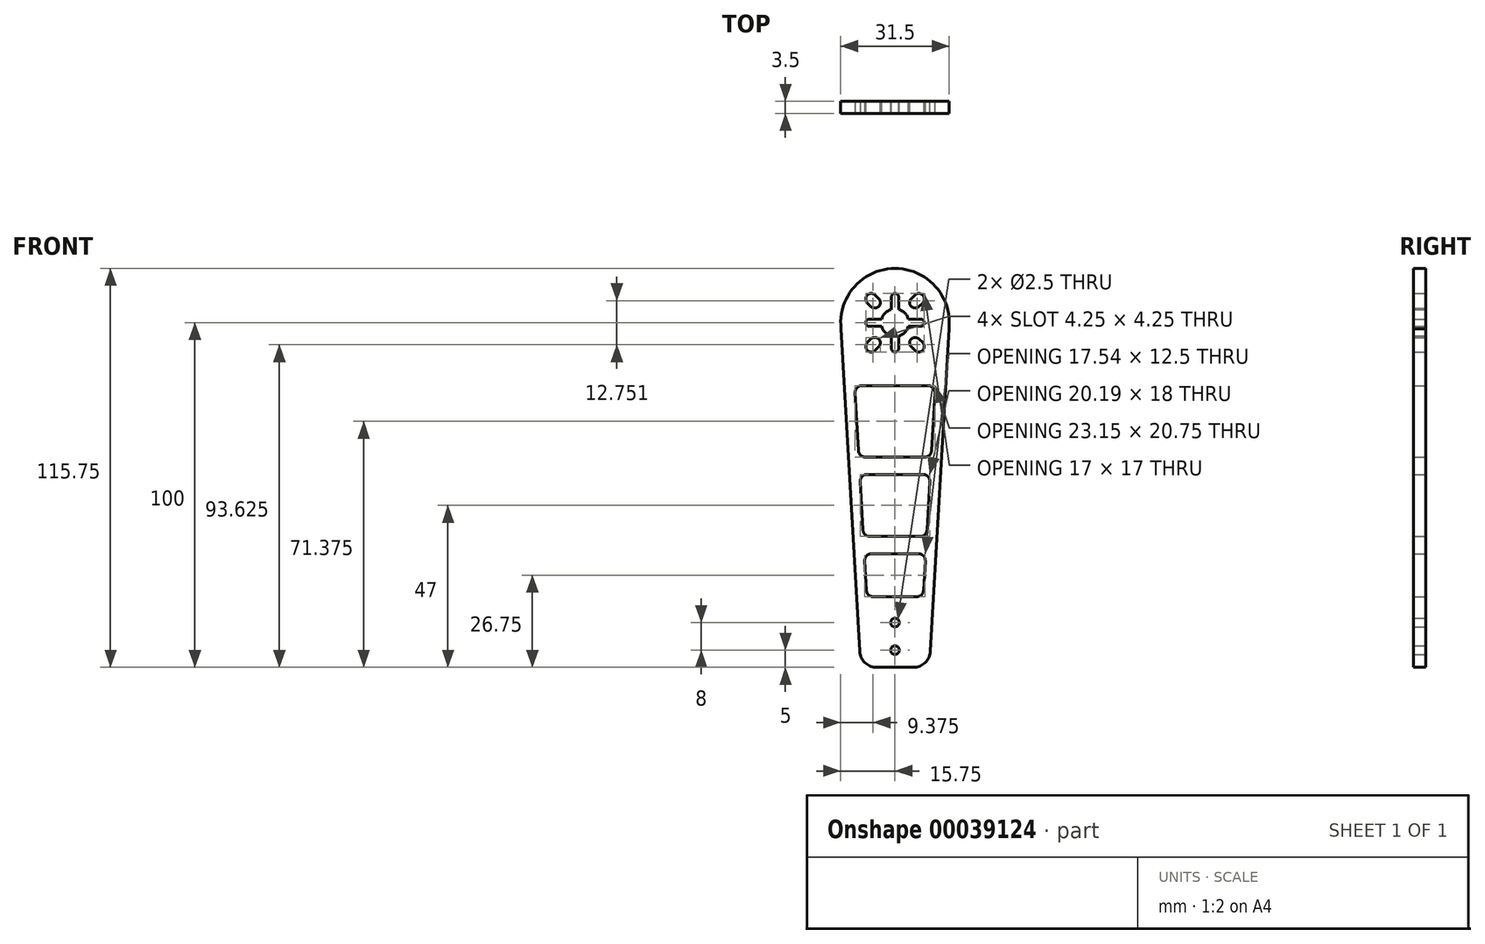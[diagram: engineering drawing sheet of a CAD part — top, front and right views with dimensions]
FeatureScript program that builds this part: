
annotation { "Feature Type Name" : "Feature", "Feature Type Description" : "" }
export const myFeature = defineFeature(function(context is Context, id is Id, definition is map)
    precondition{}
    {
        {
            var Q0;
            Q0=qCreatedBy(makeId("Front.planeOp"),FACE);
            var sketch = newSketch(context, id + "F0", { "sketchPlane" : qUnion([Q0])});
            skLineSegment(sketch, "E0", {"start": v(0, 21.72) * mm, "end": v(0, -118.47) * mm, "construction": true});
            skCircle(sketch, "E1", {"center": v(0, -87) * mm, "radius": 1.25 * mm});
            skCircle(sketch, "E2", {"center": v(0, -95) * mm, "radius": 1.25 * mm});
            skPoint(sketch, "E3.rect.middle", {"position": v(0, 0) * mm});
            skLineSegment(sketch, "E4", {"start": v(0, 0) * mm, "end": v(8.03, 8.03) * mm, "construction": true});
            skPoint(sketch, "E5.2.0", {"position": v(-6.38, -6.38) * mm});
            skPoint(sketch, "E6.rect.middle", {"position": v(6.38, 6.38) * mm});
            skLineSegment(sketch, "E7.rect.top", {"start": v(7.45, 1.05) * mm, "end": v(-7.45, 1.05) * mm});
            skLineSegment(sketch, "E7.rect.bottom", {"start": v(7.45, -1.05) * mm, "end": v(-7.45, -1.05) * mm});
            skLineSegment(sketch, "E8", {"start": v(-9.34, 0) * mm, "end": v(12.16, 0) * mm, "construction": true});
            skCircle(sketch, "E9", {"center": v(0, 0) * mm, "radius": 4 * mm});
            skPoint(sketch, "E5.1.0", {"position": v(-6.38, 6.38) * mm});
            skCircle(sketch, "E10", {"center": v(0, 0) * mm, "radius": 15.75 * mm});
            skLineSegment(sketch, "E3.rect.right", {"start": v(1.05, 7.45) * mm, "end": v(1.05, -7.45) * mm});
            skLineSegment(sketch, "E3.rect.left", {"start": v(-1.05, 7.45) * mm, "end": v(-1.05, -7.45) * mm});
            skPoint(sketch, "E5.3.0", {"position": v(6.38, -6.38) * mm});
            skArc(sketch, "E5.3.2", {"start": v(5.77, -8.03) * mm, "mid": v(8.03, -8.03) * mm, "end": v(8.03, -5.77) * mm});
            skLineSegment(sketch, "E11", {"start": v(0, 8.5) * mm, "end": v(12.03, 8.5) * mm, "construction": true});
            skArc(sketch, "E5.3.1", {"start": v(6.98, -4.72) * mm, "mid": v(4.72, -4.72) * mm, "end": v(4.72, -6.98) * mm});
            skArc(sketch, "E5.1.2", {"start": v(-5.77, 8.03) * mm, "mid": v(-8.03, 8.03) * mm, "end": v(-8.03, 5.77) * mm});
            skArc(sketch, "E5.2.2", {"start": v(-8.03, -5.77) * mm, "mid": v(-8.03, -8.03) * mm, "end": v(-5.77, -8.03) * mm});
            skArc(sketch, "E5.1.1", {"start": v(-6.98, 4.72) * mm, "mid": v(-4.72, 4.72) * mm, "end": v(-4.72, 6.98) * mm});
            skArc(sketch, "E12", {"start": v(4.72, 6.98) * mm, "mid": v(4.72, 4.72) * mm, "end": v(6.98, 4.72) * mm});
            skArc(sketch, "E5.2.1", {"start": v(-4.72, -6.98) * mm, "mid": v(-4.72, -4.72) * mm, "end": v(-6.98, -4.72) * mm});
            skArc(sketch, "E13", {"start": v(8.03, 5.77) * mm, "mid": v(8.03, 8.03) * mm, "end": v(5.77, 8.03) * mm});
            skLineSegment(sketch, "E5.1.6", {"start": v(-4.72, 6.98) * mm, "end": v(-5.77, 8.03) * mm});
            skArc(sketch, "E14", {"start": v(-1.05, -7.45) * mm, "mid": v(0, -8.5) * mm, "end": v(1.05, -7.45) * mm});
            skLineSegment(sketch, "E5.2.4", {"start": v(-6.98, -4.72) * mm, "end": v(-4.72, -6.98) * mm});
            skLineSegment(sketch, "E5.1.3", {"start": v(-5.77, 8.03) * mm, "end": v(-8.03, 5.77) * mm});
            skLineSegment(sketch, "E6.rect.bottom", {"start": v(6.98, 4.72) * mm, "end": v(8.03, 5.77) * mm});
            skLineSegment(sketch, "E6.rect.right", {"start": v(8.03, 5.77) * mm, "end": v(5.77, 8.03) * mm});
            skLineSegment(sketch, "E5.1.5", {"start": v(-6.98, 4.72) * mm, "end": v(-8.03, 5.77) * mm});
            skArc(sketch, "E15", {"start": v(1.05, 7.45) * mm, "mid": v(0, 8.5) * mm, "end": v(-1.05, 7.45) * mm});
            skLineSegment(sketch, "E5.2.3", {"start": v(-8.03, -5.77) * mm, "end": v(-5.77, -8.03) * mm});
            skLineSegment(sketch, "E5.3.6", {"start": v(4.72, -6.98) * mm, "end": v(5.77, -8.03) * mm});
            skLineSegment(sketch, "E6.rect.left", {"start": v(6.98, 4.72) * mm, "end": v(4.72, 6.98) * mm});
            skLineSegment(sketch, "E5.2.6", {"start": v(-6.98, -4.72) * mm, "end": v(-8.03, -5.77) * mm});
            skLineSegment(sketch, "E5.3.4", {"start": v(4.72, -6.98) * mm, "end": v(6.98, -4.72) * mm});
            skLineSegment(sketch, "E5.1.4", {"start": v(-4.72, 6.98) * mm, "end": v(-6.98, 4.72) * mm});
            skArc(sketch, "E16", {"start": v(7.45, -1.05) * mm, "mid": v(8.5, 0) * mm, "end": v(7.45, 1.05) * mm});
            skLineSegment(sketch, "E5.3.5", {"start": v(6.98, -4.72) * mm, "end": v(8.03, -5.77) * mm});
            skLineSegment(sketch, "E5.2.5", {"start": v(-4.72, -6.98) * mm, "end": v(-5.77, -8.03) * mm});
            skLineSegment(sketch, "E5.3.3", {"start": v(5.77, -8.03) * mm, "end": v(8.03, -5.77) * mm});
            skLineSegment(sketch, "E3.rect.top", {"start": v(-1.05, -7.45) * mm, "end": v(1.05, -7.45) * mm});
            skLineSegment(sketch, "E7.rect.right", {"start": v(-7.45, -1.05) * mm, "end": v(-7.45, 1.05) * mm});
            skLineSegment(sketch, "E7.rect.left", {"start": v(7.45, -1.05) * mm, "end": v(7.45, 1.05) * mm});
            skArc(sketch, "E17", {"start": v(-7.45, 1.05) * mm, "mid": v(-8.5, 0) * mm, "end": v(-7.45, -1.05) * mm});
            skLineSegment(sketch, "E6.rect.top", {"start": v(4.72, 6.98) * mm, "end": v(5.77, 8.03) * mm});
            skLineSegment(sketch, "E3.rect.bottom", {"start": v(-1.05, 7.45) * mm, "end": v(1.05, 7.45) * mm});
            skLineSegment(sketch, "E18", {"start": v(-15.75, 0) * mm, "end": v(-10, -100) * mm});
            skLineSegment(sketch, "E19", {"start": v(0, -44) * mm, "end": v(-10.22, -44) * mm});
            skLineSegment(sketch, "E20", {"start": v(-10.22, -44) * mm, "end": v(-9.18, -62) * mm});
            skLineSegment(sketch, "E21", {"start": v(-9.18, -62) * mm, "end": v(0, -62) * mm});
            skPoint(sketch, "E21.endSnap0", {"position": v(0, -48.38) * mm});
            skLineSegment(sketch, "E22", {"start": v(0, -67) * mm, "end": v(-8.9, -67) * mm});
            skLineSegment(sketch, "E23", {"start": v(-8.9, -67) * mm, "end": v(-8.17, -79.5) * mm});
            skLineSegment(sketch, "E24", {"start": v(-8.17, -79.5) * mm, "end": v(0, -79.5) * mm});
            skLineSegment(sketch, "E25.MirrorCS", {"start": v(0, -67) * mm, "end": v(8.9, -67) * mm});
            skLineSegment(sketch, "E26.MirrorCS", {"start": v(8.9, -67) * mm, "end": v(8.17, -79.5) * mm});
            skLineSegment(sketch, "E27.MirrorCS", {"start": v(8.17, -79.5) * mm, "end": v(0, -79.5) * mm});
            skLineSegment(sketch, "E28.MirrorCS", {"start": v(9.18, -62) * mm, "end": v(0, -62) * mm});
            skLineSegment(sketch, "E29.MirrorCS", {"start": v(0, -44) * mm, "end": v(10.22, -44) * mm});
            skLineSegment(sketch, "E30.MirrorCS", {"start": v(10.22, -44) * mm, "end": v(9.18, -62) * mm});
            skLineSegment(sketch, "E31", {"start": v(0, -18.25) * mm, "end": v(-11.7, -18.25) * mm});
            skLineSegment(sketch, "E32", {"start": v(-11.7, -18.25) * mm, "end": v(-10.5, -39) * mm});
            skLineSegment(sketch, "E33", {"start": v(-10.5, -39) * mm, "end": v(0, -39) * mm});
            skLineSegment(sketch, "E34.MirrorCS", {"start": v(10.5, -39) * mm, "end": v(0, -39) * mm});
            skLineSegment(sketch, "E35.MirrorCS", {"start": v(0, -18.25) * mm, "end": v(11.7, -18.25) * mm});
            skLineSegment(sketch, "E36.MirrorCS", {"start": v(11.7, -18.25) * mm, "end": v(10.5, -39) * mm});
            skLineSegment(sketch, "E37", {"start": v(-10, -100) * mm, "end": v(0, -100) * mm});
            skLineSegment(sketch, "E38.MirrorCS", {"start": v(15.75, 0) * mm, "end": v(10, -100) * mm});
            skLineSegment(sketch, "E39.MirrorCS", {"start": v(10, -100) * mm, "end": v(0, -100) * mm});
            skSolve(sketch);
        }
        {
            var Q0;
            Q0 = qSketchRegion(id + "F0", true);
            extrude(context, id + "F1", {"entities" : qUnion([Q0]), "depth" : 3.5 * mm});
        }
        {
            var Q0;
            Q0=makeQuery(id+"F1.opExtrude","SWEPT_EDGE",EDGE,{"disambiguationData":[OSD([sQuery(id+"F0.wireOp",EDGE,"E18"),sQuery(id+"F0.wireOp",EDGE,"E37")])]});
            var Q1;
            Q1=makeQuery(id+"F1.opExtrude","SWEPT_EDGE",EDGE,{"disambiguationData":[OSD([sQuery(id+"F0.wireOp",EDGE,"E38.MirrorCS"),sQuery(id+"F0.wireOp",EDGE,"E39.MirrorCS")])]});
            fillet(context, id + "F2", {"entities" : qUnion([Q0, Q1]), "radius" : 5 * mm, "tangentPropagation" : true, "allowEdgeOverflow" : false});
        }
        {
            var Q0;
            Q0=makeQuery(id+"F1.opExtrude","SWEPT_EDGE",EDGE,{"disambiguationData":[OSD([sQuery(id+"F0.wireOp",EDGE,"E32"),sQuery(id+"F0.wireOp",EDGE,"E33")])]});
            var Q1;
            Q1=makeQuery(id+"F1.opExtrude","SWEPT_EDGE",EDGE,{"disambiguationData":[OSD([sQuery(id+"F0.wireOp",EDGE,"E20"),sQuery(id+"F0.wireOp",EDGE,"E21")])]});
            var Q2;
            Q2=makeQuery(id+"F1.opExtrude","SWEPT_EDGE",EDGE,{"disambiguationData":[OSD([sQuery(id+"F0.wireOp",EDGE,"E23"),sQuery(id+"F0.wireOp",EDGE,"E24")])]});
            var Q3;
            Q3=makeQuery(id+"F1.opExtrude","SWEPT_EDGE",EDGE,{"disambiguationData":[OSD([sQuery(id+"F0.wireOp",EDGE,"E22"),sQuery(id+"F0.wireOp",EDGE,"E23")])]});
            var Q4;
            Q4=makeQuery(id+"F1.opExtrude","SWEPT_EDGE",EDGE,{"disambiguationData":[OSD([sQuery(id+"F0.wireOp",EDGE,"E19"),sQuery(id+"F0.wireOp",EDGE,"E20")])]});
            var Q5;
            Q5=makeQuery(id+"F1.opExtrude","SWEPT_EDGE",EDGE,{"disambiguationData":[OSD([sQuery(id+"F0.wireOp",EDGE,"E31"),sQuery(id+"F0.wireOp",EDGE,"E32")])]});
            var Q6;
            Q6=makeQuery(id+"F1.opExtrude","SWEPT_EDGE",EDGE,{"disambiguationData":[OSD([sQuery(id+"F0.wireOp",EDGE,"E35.MirrorCS"),sQuery(id+"F0.wireOp",EDGE,"E36.MirrorCS")])]});
            var Q7;
            Q7=makeQuery(id+"F1.opExtrude","SWEPT_EDGE",EDGE,{"disambiguationData":[OSD([sQuery(id+"F0.wireOp",EDGE,"E29.MirrorCS"),sQuery(id+"F0.wireOp",EDGE,"E30.MirrorCS")])]});
            var Q8;
            Q8=makeQuery(id+"F1.opExtrude","SWEPT_EDGE",EDGE,{"disambiguationData":[OSD([sQuery(id+"F0.wireOp",EDGE,"E25.MirrorCS"),sQuery(id+"F0.wireOp",EDGE,"E26.MirrorCS")])]});
            var Q9;
            Q9=makeQuery(id+"F1.opExtrude","SWEPT_EDGE",EDGE,{"disambiguationData":[OSD([sQuery(id+"F0.wireOp",EDGE,"E34.MirrorCS"),sQuery(id+"F0.wireOp",EDGE,"E36.MirrorCS")])]});
            var Q10;
            Q10=makeQuery(id+"F1.opExtrude","SWEPT_EDGE",EDGE,{"disambiguationData":[OSD([sQuery(id+"F0.wireOp",EDGE,"E28.MirrorCS"),sQuery(id+"F0.wireOp",EDGE,"E30.MirrorCS")])]});
            var Q11;
            Q11=makeQuery(id+"F1.opExtrude","SWEPT_EDGE",EDGE,{"disambiguationData":[OSD([sQuery(id+"F0.wireOp",EDGE,"E26.MirrorCS"),sQuery(id+"F0.wireOp",EDGE,"E27.MirrorCS")])]});
            fillet(context, id + "F3", {"entities" : qUnion([Q0, Q1, Q2, Q3, Q4, Q5, Q6, Q7, Q8, Q9, Q10, Q11]), "radius" : 2 * mm, "tangentPropagation" : true, "allowEdgeOverflow" : false});
        }
    });
